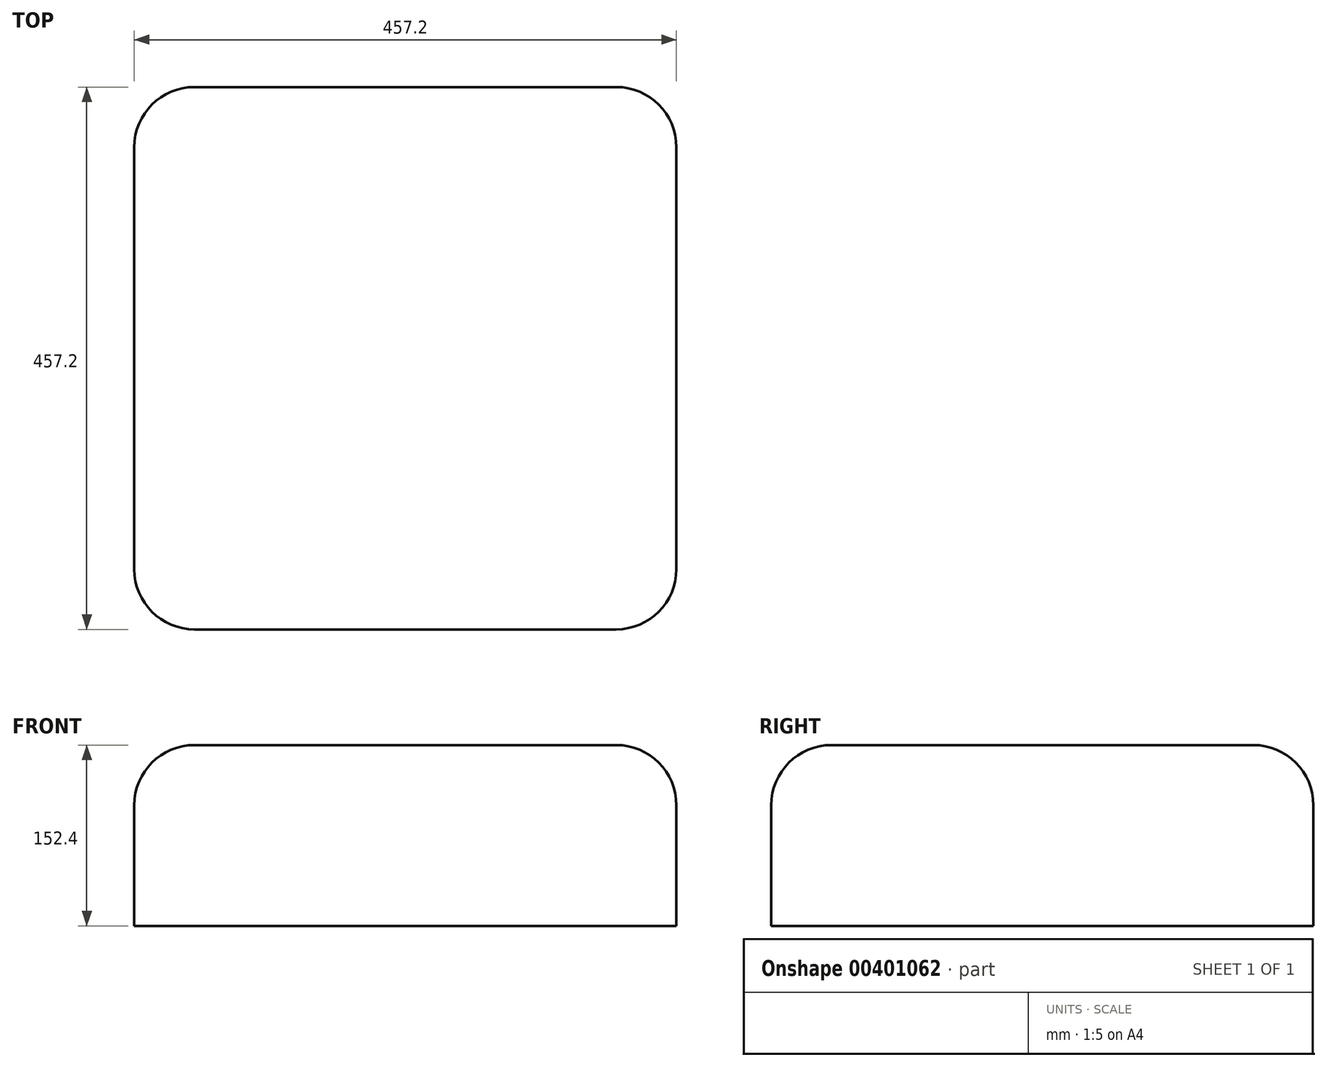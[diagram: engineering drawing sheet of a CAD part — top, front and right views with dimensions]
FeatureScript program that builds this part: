
annotation { "Feature Type Name" : "Feature", "Feature Type Description" : "" }
export const myFeature = defineFeature(function(context is Context, id is Id, definition is map)
    precondition{}
    {
        {
            var Q0;
            Q0=qCreatedBy(makeId("Top.planeOp"),FACE);
            var sketch = newSketch(context, id + "F0", { "sketchPlane" : qUnion([Q0])});
            skLineSegment(sketch, "E0.bottom", {"start": v(-228.6, 228.6) * mm, "end": v(228.6, 228.6) * mm});
            skLineSegment(sketch, "E0.top", {"start": v(-228.6, -228.6) * mm, "end": v(228.6, -228.6) * mm});
            skLineSegment(sketch, "E0.left", {"start": v(-228.6, 228.6) * mm, "end": v(-228.6, -228.6) * mm});
            skLineSegment(sketch, "E0.right", {"start": v(228.6, 228.6) * mm, "end": v(228.6, -228.6) * mm});
            skSolve(sketch);
        }
        {
            var Q0;
            Q0=makeQuery(id+"F0.imprint","IMPRINT",FACE,{"disambiguationData":[TD([[makeQuery(id+"F0.imprint","IMPRINT",EDGE,{"derivedFrom":sQuery(id+"F0.wireOp",EDGE,"E0.bottom")}),-1.0]])]});
            extrude(context, id + "F1", {"entities" : qUnion([Q0]), "depth" : 152.4 * mm});
        }
        {
            var Q0;
            Q0=makeQuery(id+"F1.opExtrude","SWEPT_EDGE",EDGE,{"disambiguationData":[OSD([sQuery(id+"F0.wireOp",EDGE,"E0.top"),sQuery(id+"F0.wireOp",EDGE,"E0.left")])]});
            var Q1;
            Q1=makeQuery(id+"F1.opExtrude","CAP_EDGE",EDGE,{"disambiguationData":[OSD([sQuery(id+"F0.wireOp",EDGE,"E0.left")])],"isStart":false});
            var Q2;
            Q2=makeQuery(id+"F1.opExtrude","CAP_EDGE",EDGE,{"disambiguationData":[OSD([sQuery(id+"F0.wireOp",EDGE,"E0.top")])],"isStart":false});
            var Q3;
            Q3=makeQuery(id+"F1.opExtrude","SWEPT_EDGE",EDGE,{"disambiguationData":[OSD([sQuery(id+"F0.wireOp",EDGE,"E0.top"),sQuery(id+"F0.wireOp",EDGE,"E0.right")])]});
            var Q4;
            Q4=makeQuery(id+"F1.opExtrude","CAP_EDGE",EDGE,{"disambiguationData":[OSD([sQuery(id+"F0.wireOp",EDGE,"E0.right")])],"isStart":false});
            var Q5;
            Q5=makeQuery(id+"F1.opExtrude","SWEPT_EDGE",EDGE,{"disambiguationData":[OSD([sQuery(id+"F0.wireOp",EDGE,"E0.bottom"),sQuery(id+"F0.wireOp",EDGE,"E0.right")])]});
            var Q6;
            Q6=makeQuery(id+"F1.opExtrude","CAP_EDGE",EDGE,{"disambiguationData":[OSD([sQuery(id+"F0.wireOp",EDGE,"E0.bottom")])],"isStart":false});
            var Q7;
            Q7=makeQuery(id+"F1.opExtrude","SWEPT_EDGE",EDGE,{"disambiguationData":[OSD([sQuery(id+"F0.wireOp",EDGE,"E0.bottom"),sQuery(id+"F0.wireOp",EDGE,"E0.left")])]});
            fillet(context, id + "F2", {"entities" : qUnion([Q0, Q1, Q2, Q3, Q4, Q5, Q6, Q7]), "radius" : 50.8 * mm, "tangentPropagation" : true, "allowEdgeOverflow" : false});
        }
    });
